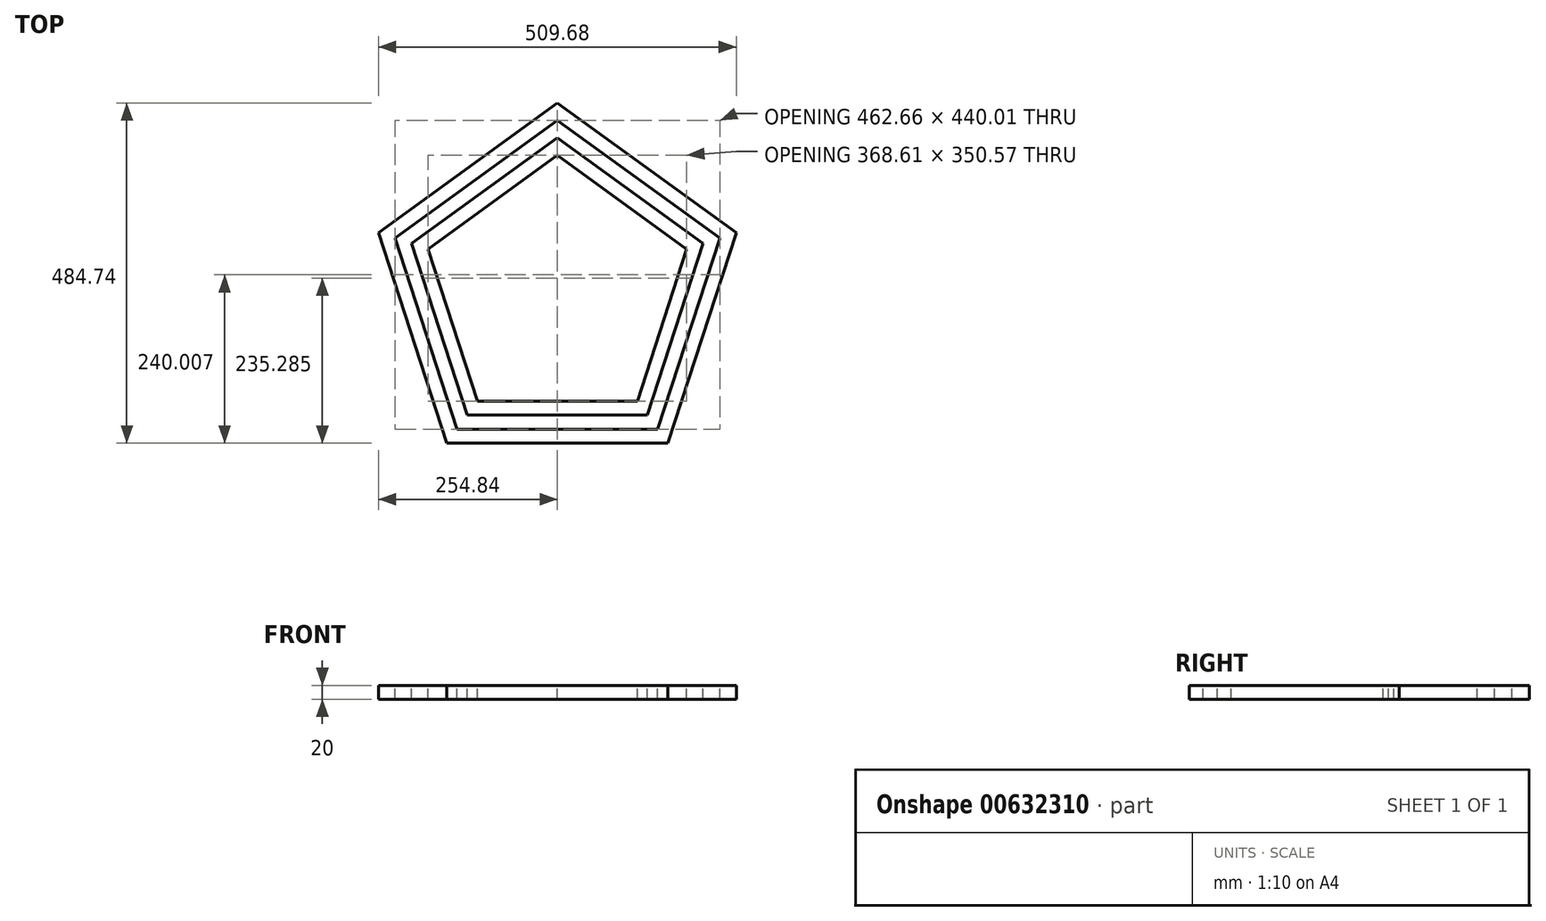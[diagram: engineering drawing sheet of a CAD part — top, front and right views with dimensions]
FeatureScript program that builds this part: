
annotation { "Feature Type Name" : "Feature", "Feature Type Description" : "" }
export const myFeature = defineFeature(function(context is Context, id is Id, definition is map)
    precondition{}
    {
        {
            var Q0;
            Q0=qCreatedBy(makeId("Top.planeOp"),FACE);
            var sketch = newSketch(context, id + "F0", { "sketchPlane" : qUnion([Q0])});
            skCircle(sketch, "E0.cCircle", {"center": v(0, 0) * mm, "radius": 267.96 * mm, "construction": true});
            skLineSegment(sketch, "E0.0", {"start": v(157.5, -216.78) * mm, "end": v(-157.5, -216.78) * mm});
            skLineSegment(sketch, "E0.1", {"start": v(-157.5, -216.78) * mm, "end": v(-254.84, 82.8) * mm});
            skLineSegment(sketch, "E0.2", {"start": v(-254.84, 82.8) * mm, "end": v(0, 267.96) * mm});
            skLineSegment(sketch, "E0.3", {"start": v(0, 267.96) * mm, "end": v(254.84, 82.8) * mm});
            skLineSegment(sketch, "E0.4", {"start": v(254.84, 82.8) * mm, "end": v(157.5, -216.78) * mm});
            skLineSegment(sketch, "E1.0", {"start": v(0, 243.23) * mm, "end": v(231.33, 75.16) * mm});
            skLineSegment(sketch, "E1.1", {"start": v(-231.33, 75.16) * mm, "end": v(0, 243.23) * mm});
            skLineSegment(sketch, "E1.2", {"start": v(231.33, 75.16) * mm, "end": v(142.97, -196.78) * mm});
            skLineSegment(sketch, "E1.3", {"start": v(142.97, -196.78) * mm, "end": v(-142.97, -196.78) * mm});
            skLineSegment(sketch, "E1.4", {"start": v(-142.97, -196.78) * mm, "end": v(-231.33, 75.16) * mm});
            skLineSegment(sketch, "E2.0", {"start": v(0, 218.51) * mm, "end": v(207.82, 67.52) * mm});
            skLineSegment(sketch, "E2.1", {"start": v(-207.82, 67.52) * mm, "end": v(0, 218.51) * mm});
            skLineSegment(sketch, "E2.2", {"start": v(207.82, 67.52) * mm, "end": v(128.44, -176.78) * mm});
            skLineSegment(sketch, "E2.3", {"start": v(128.44, -176.78) * mm, "end": v(-128.44, -176.78) * mm});
            skLineSegment(sketch, "E2.4", {"start": v(-128.44, -176.78) * mm, "end": v(-207.82, 67.52) * mm});
            skLineSegment(sketch, "E3.0", {"start": v(0, 193.8) * mm, "end": v(184.3, 59.88) * mm});
            skLineSegment(sketch, "E3.1", {"start": v(-184.3, 59.88) * mm, "end": v(0, 193.8) * mm});
            skLineSegment(sketch, "E3.2", {"start": v(184.3, 59.88) * mm, "end": v(113.9, -156.78) * mm});
            skLineSegment(sketch, "E3.3", {"start": v(113.9, -156.78) * mm, "end": v(-113.9, -156.78) * mm});
            skLineSegment(sketch, "E3.4", {"start": v(-113.9, -156.78) * mm, "end": v(-184.3, 59.88) * mm});
            skLineSegment(sketch, "E4", {"start": v(-168.13, -54.63) * mm, "end": v(-149.1, -48.45) * mm, "construction": true});
            skLineSegment(sketch, "E5", {"start": v(-158.62, -51.54) * mm, "end": v(-174.07, -3.99) * mm, "construction": true});
            skPoint(sketch, "E6", {"position": v(-174.07, -3.99) * mm});
            skPoint(sketch, "E7.1.0", {"position": v(-48.07, -166.74) * mm});
            skPoint(sketch, "E7.2.0", {"position": v(145.66, -97.2) * mm});
            skPoint(sketch, "E7.3.0", {"position": v(139.4, 108.53) * mm});
            skPoint(sketch, "E7.4.0", {"position": v(-58.21, 166.14) * mm});
            skPoint(sketch, "E7.center", {"position": v(0.94, 1.35) * mm});
            skLineSegment(sketch, "E8", {"start": v(-48.07, -156.78) * mm, "end": v(-48.07, -176.78) * mm, "construction": true});
            skPoint(sketch, "E9", {"position": v(-48.07, -196.78) * mm});
            skLineSegment(sketch, "E10.trimOffspring", {"start": v(-48.07, -196.78) * mm, "end": v(-48.07, -216.78) * mm, "construction": true});
            skPoint(sketch, "E11", {"position": v(-48.07, -206.78) * mm});
            skSolve(sketch);
        }
        {
            var Q0;
            Q0=makeQuery(id+"F0.imprint","IMPRINT",FACE,{"disambiguationData":[TD([[makeQuery(id+"F0.imprint","IMPRINT",EDGE,{"derivedFrom":sQuery(id+"F0.wireOp",EDGE,"E0.0")}),-1.0]])]});
            var Q1;
            Q1=makeQuery(id+"F0.imprint","IMPRINT",FACE,{"disambiguationData":[TD([[makeQuery(id+"F0.imprint","IMPRINT",EDGE,{"derivedFrom":sQuery(id+"F0.wireOp",EDGE,"E2.0")}),-1.0]])]});
            extrude(context, id + "F1", {"entities" : qUnion([Q0, Q1]), "oppositeDirection" : true, "depth" : 20 * mm, "offsetDistance" : 25 * mm});
        }
    });
